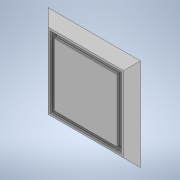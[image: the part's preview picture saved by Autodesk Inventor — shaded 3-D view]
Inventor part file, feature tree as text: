
AUTODESK INVENTOR PART (.ipt)
format: ipt  version: 2021 (Build 250183000, 183)  size: 128,512 bytes
history: native  units: in
note: dims shown in document units (in); Inventor stores cm internally (conversion verified against a paired STEP export)
features: extrude x2, chamfer x2, sketch x2, projected_geometry x1
ambient origin geometry x8: Origin, YZ Plane, XZ Plane, XY Plane, X Axis, Y Axis, Z Axis, Center Point
bodies: Solid1 (feature_tree)
feature tree (7):
  extrude  "Extrusion1"  Depth=0.1575in
  chamfer  "Chamfer1"  Distance=0.1575in
  extrude  "Extrusion2"  Depth=0.0787in
  chamfer  "Chamfer2"  Distance=0.0394in
  sketch  "Sketch1"  dims[d0=1.7323in d1=1.7323in d2=0.1575in d3=0.0in]
  sketch  "Sketch2"  dims[d4=0.1575in d5=0.0787in d6=45.0deg d7=0.0394in d8=0.0394in d9=1.3386in d10=1.3386in d11=0.0787in d12=0.0787in d13=1.1811in d14=1.1811in d15=0.0787in d16=0.0in d17=0.0394in d18=0.0787in d19=45.0deg]
  projected_geometry  "Projected Loop1"
